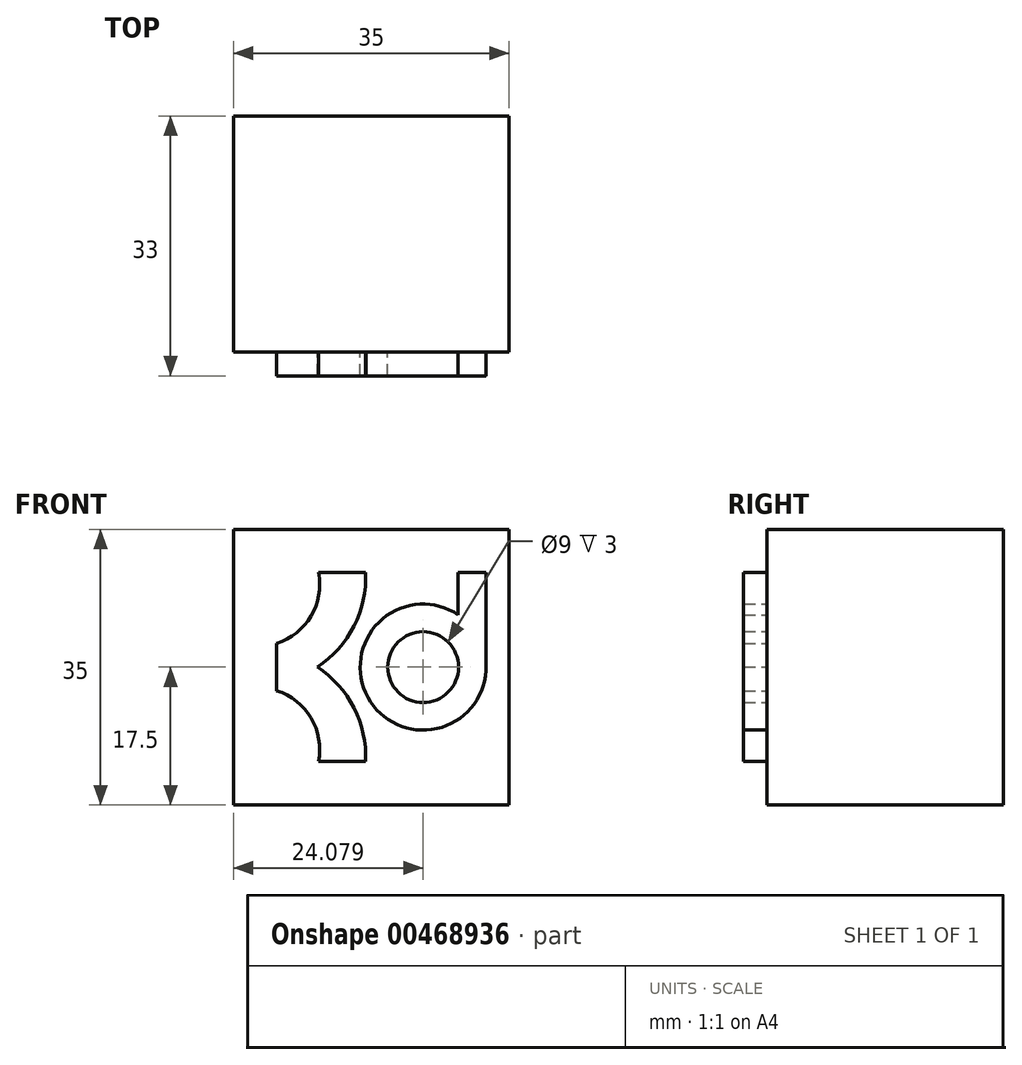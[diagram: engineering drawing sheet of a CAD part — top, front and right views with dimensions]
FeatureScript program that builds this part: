
annotation { "Feature Type Name" : "Feature", "Feature Type Description" : "" }
export const myFeature = defineFeature(function(context is Context, id is Id, definition is map)
    precondition{}
    {
        {
            var Q0;
            Q0=qCreatedBy(makeId("Front.planeOp"),FACE);
            var sketch = newSketch(context, id + "F0", { "sketchPlane" : qUnion([Q0])});
            skLineSegment(sketch, "E0.bottom", {"start": v(17.5, -17.5) * mm, "end": v(-17.5, -17.5) * mm});
            skLineSegment(sketch, "E0.top", {"start": v(17.5, 17.5) * mm, "end": v(-17.5, 17.5) * mm});
            skLineSegment(sketch, "E0.left", {"start": v(17.5, -17.5) * mm, "end": v(17.5, 17.5) * mm});
            skLineSegment(sketch, "E0.right", {"start": v(-17.5, -17.5) * mm, "end": v(-17.5, 17.5) * mm});
            skPoint(sketch, "E0.middle", {"position": v(0, 0) * mm});
            skSolve(sketch);
        }
        {
            var Q0;
            Q0 = qSketchRegion(id + "F0", true);
            extrude(context, id + "F1", {"entities" : qUnion([Q0]), "endBound" : BoundingType.SYMMETRIC, "depth" : 30 * mm});
        }
        {
            var Q0;
            Q0=makeQuery(id+"F1.opExtrude","CAP_FACE",FACE,{"disambiguationData":[OSD([sQuery(id+"F0.wireOp",EDGE,"E0.bottom"),sQuery(id+"F0.wireOp",EDGE,"E0.top"),sQuery(id+"F0.wireOp",EDGE,"E0.left"),sQuery(id+"F0.wireOp",EDGE,"E0.right")])],"isStart":false});
            var sketch = newSketch(context, id + "F2", { "sketchPlane" : qUnion([Q0])});
            skLineSegment(sketch, "E1", {"start": v(-12.06, 0) * mm, "end": v(-12.06, 3) * mm});
            skArc(sketch, "E2", {"start": v(-12.06, 3) * mm, "mid": v(-7.65, 6.47) * mm, "end": v(-6.71, 12) * mm});
            skLineSegment(sketch, "E3", {"start": v(-6.71, 12) * mm, "end": v(-0.71, 12) * mm});
            skArc(sketch, "E4", {"start": v(-6.84, 0) * mm, "mid": v(-2.2, 5.2) * mm, "end": v(-0.71, 12) * mm});
            skArc(sketch, "E5.MirrorCS", {"start": v(-6.84, 0) * mm, "mid": v(-2.2, -5.2) * mm, "end": v(-0.71, -12) * mm});
            skArc(sketch, "E6.MirrorCS", {"start": v(-12.06, -3) * mm, "mid": v(-7.65, -6.47) * mm, "end": v(-6.71, -12) * mm});
            skLineSegment(sketch, "E7.MirrorCS", {"start": v(-12.06, 0) * mm, "end": v(-12.06, -3) * mm});
            skLineSegment(sketch, "E8.MirrorCS", {"start": v(-6.71, -12) * mm, "end": v(-0.71, -12) * mm});
            skCircle(sketch, "E9", {"center": v(6.58, 0) * mm, "radius": 8 * mm});
            skCircle(sketch, "E10", {"center": v(6.58, 0) * mm, "radius": 4.5 * mm});
            skLineSegment(sketch, "E11.bottom", {"start": v(11.04, -0.56) * mm, "end": v(14.54, -0.56) * mm});
            skLineSegment(sketch, "E11.top", {"start": v(11.04, 12) * mm, "end": v(14.54, 12) * mm});
            skLineSegment(sketch, "E11.left", {"start": v(11.04, -0.56) * mm, "end": v(11.04, 12) * mm});
            skLineSegment(sketch, "E11.right", {"start": v(14.54, -0.56) * mm, "end": v(14.54, 12) * mm});
            skLineSegment(sketch, "E12", {"start": v(14.54, -0.56) * mm, "end": v(14.67, -0.56) * mm});
            skSolve(sketch);
        }
        {
            var Q0;
            Q0=makeQuery(id+"F2.imprint","IMPRINT",FACE,{"disambiguationData":[TD([[makeQuery(id+"F2.imprint","IMPRINT",EDGE,{"derivedFrom":sQuery(id+"F2.wireOp",EDGE,"E1")}),1.0]])]});
            var sketch = newSketch(context, id + "F3", { "sketchPlane" : qUnion([Q0])});
            skLineSegment(sketch, "E13.0", {"start": v(-12.06, 0) * mm, "end": v(-12.06, 3) * mm});
            skArc(sketch, "E13.1", {"start": v(-12.06, 3) * mm, "mid": v(-7.65, 6.47) * mm, "end": v(-6.71, 12) * mm});
            skLineSegment(sketch, "E13.2", {"start": v(-6.71, 12) * mm, "end": v(-0.71, 12) * mm});
            skArc(sketch, "E13.3", {"start": v(-6.84, 0) * mm, "mid": v(-2.2, 5.2) * mm, "end": v(-0.71, 12) * mm});
            skArc(sketch, "E13.4", {"start": v(-6.84, 0) * mm, "mid": v(-2.2, -5.2) * mm, "end": v(-0.71, -12) * mm});
            skArc(sketch, "E13.5", {"start": v(-12.06, -3) * mm, "mid": v(-7.65, -6.47) * mm, "end": v(-6.71, -12) * mm});
            skLineSegment(sketch, "E13.6", {"start": v(-12.06, 0) * mm, "end": v(-12.06, -3) * mm});
            skLineSegment(sketch, "E13.7", {"start": v(-6.71, -12) * mm, "end": v(-0.71, -12) * mm});
            skArc(sketch, "E13.8", {"start": v(11.04, 6.64) * mm, "mid": v(-0.6, -3.51) * mm, "end": v(14.56, -0.56) * mm});
            skCircle(sketch, "E13.9", {"center": v(6.58, 0) * mm, "radius": 4.5 * mm});
            skLineSegment(sketch, "E13.11", {"start": v(11.04, 12) * mm, "end": v(14.54, 12) * mm});
            skLineSegment(sketch, "E13.13", {"start": v(14.54, -0.56) * mm, "end": v(14.54, 12) * mm});
            skLineSegment(sketch, "E13.14", {"start": v(14.54, -0.56) * mm, "end": v(14.56, -0.56) * mm});
            skPoint(sketch, "E13.10.end.orphan", {"position": v(14.54, -0.56) * mm});
            skPoint(sketch, "E13.10.start.orphan", {"position": v(11.04, -0.56) * mm});
            skLineSegment(sketch, "E14.trimOffspring", {"start": v(11.04, 6.64) * mm, "end": v(11.04, 12) * mm});
            skPoint(sketch, "E13.12.start.orphan", {"position": v(11.04, -0.56) * mm});
            skPoint(sketch, "E15.orphan", {"position": v(14.67, -0.56) * mm});
            skSolve(sketch);
        }
        {
            var Q0;
            Q0 = qSketchRegion(id + "F3", true);
            extrude(context, id + "F4", {"entities" : qUnion([Q0]), "operationType" : NewBodyOperationType.ADD, "depth" : 3 * mm});
        }
        {
            var Q0;
            Q0=makeQuery(id+"F4.opExtrude","SWEPT_EDGE",EDGE,{"disambiguationData":[OSD([sQuery(id+"F3.wireOp",EDGE,"E13.13"),sQuery(id+"F3.wireOp",EDGE,"E13.14")])]});
            fillet(context, id + "F5", {"entities" : qUnion([Q0]), "radius" : 5 * mm, "tangentPropagation" : true, "allowEdgeOverflow" : false});
        }
        {
            var Q0;
            Q0=makeQuery(id+"F5.opFillet","BLEND_EDGE",EDGE,{"blendedFrom":[makeQuery(id+"F4.opExtrude","SWEPT_EDGE",EDGE,{"disambiguationData":[OSD([sQuery(id+"F3.wireOp",EDGE,"E13.13"),sQuery(id+"F3.wireOp",EDGE,"E13.14")])]}),makeQuery(id+"F4.opExtrude","SWEPT_FACE",FACE,{"disambiguationData":[OSD([sQuery(id+"F3.wireOp",EDGE,"E13.8")])]})],"blendedInto":[makeQuery(id+"F4.opExtrude","SWEPT_FACE",FACE,{"disambiguationData":[OSD([sQuery(id+"F3.wireOp",EDGE,"E13.8")])]})]});
            fillet(context, id + "F6", {"entities" : qUnion([Q0]), "radius" : 5 * mm, "tangentPropagation" : true, "allowEdgeOverflow" : false});
        }
    });
